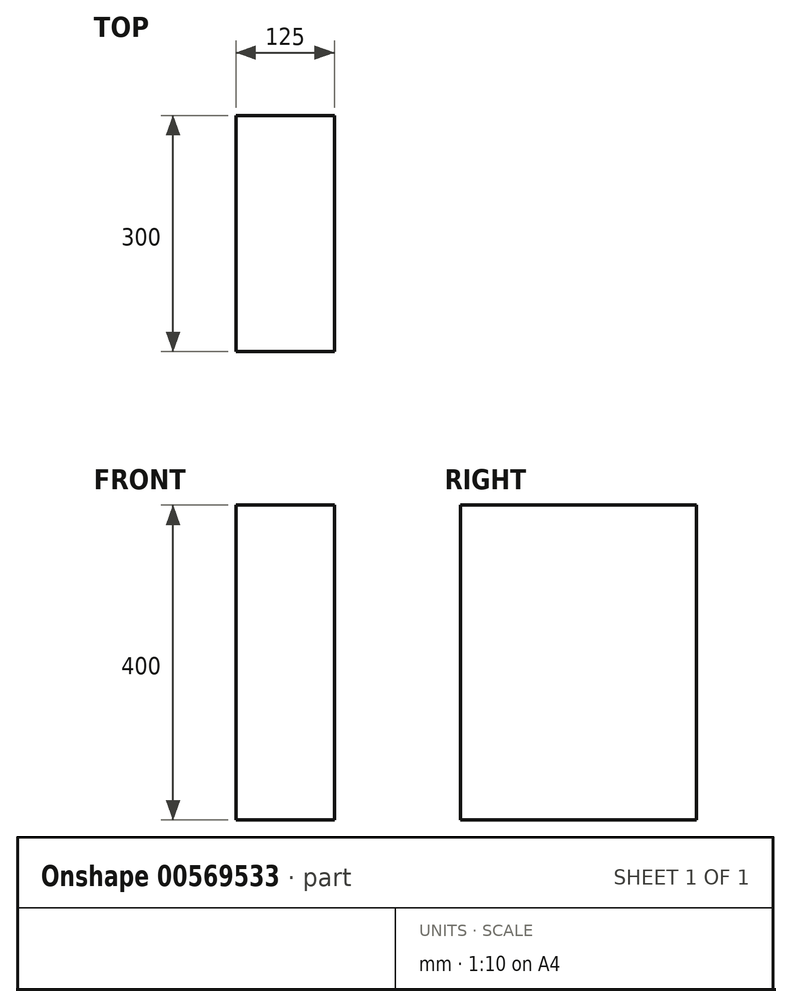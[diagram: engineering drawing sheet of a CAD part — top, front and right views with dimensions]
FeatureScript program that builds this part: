
annotation { "Feature Type Name" : "Feature", "Feature Type Description" : "" }
export const myFeature = defineFeature(function(context is Context, id is Id, definition is map)
    precondition{}
    {
        {
            var Q0;
            Q0=qCreatedBy(makeId("Right.planeOp"),FACE);
            var sketch = newSketch(context, id + "F0", { "sketchPlane" : qUnion([Q0])});
            skLineSegment(sketch, "E0.bottom", {"start": v(136.33, 212.06) * mm, "end": v(-163.67, 212.06) * mm});
            skLineSegment(sketch, "E0.top", {"start": v(136.33, -187.94) * mm, "end": v(-163.67, -187.94) * mm});
            skLineSegment(sketch, "E0.left", {"start": v(136.33, 212.06) * mm, "end": v(136.33, -187.94) * mm});
            skLineSegment(sketch, "E0.right", {"start": v(-163.67, 212.06) * mm, "end": v(-163.67, -187.94) * mm});
            skSolve(sketch);
        }
        {
            var Q0;
            Q0=makeQuery(id+"F0.imprint","IMPRINT",FACE,{"disambiguationData":[TD([[makeQuery(id+"F0.imprint","IMPRINT",EDGE,{"derivedFrom":sQuery(id+"F0.wireOp",EDGE,"E0.bottom")}),1.0]])]});
            extrude(context, id + "F1", {"entities" : qUnion([Q0]), "depth" : 125 * mm, "offsetDistance" : 25 * mm});
        }
    });
